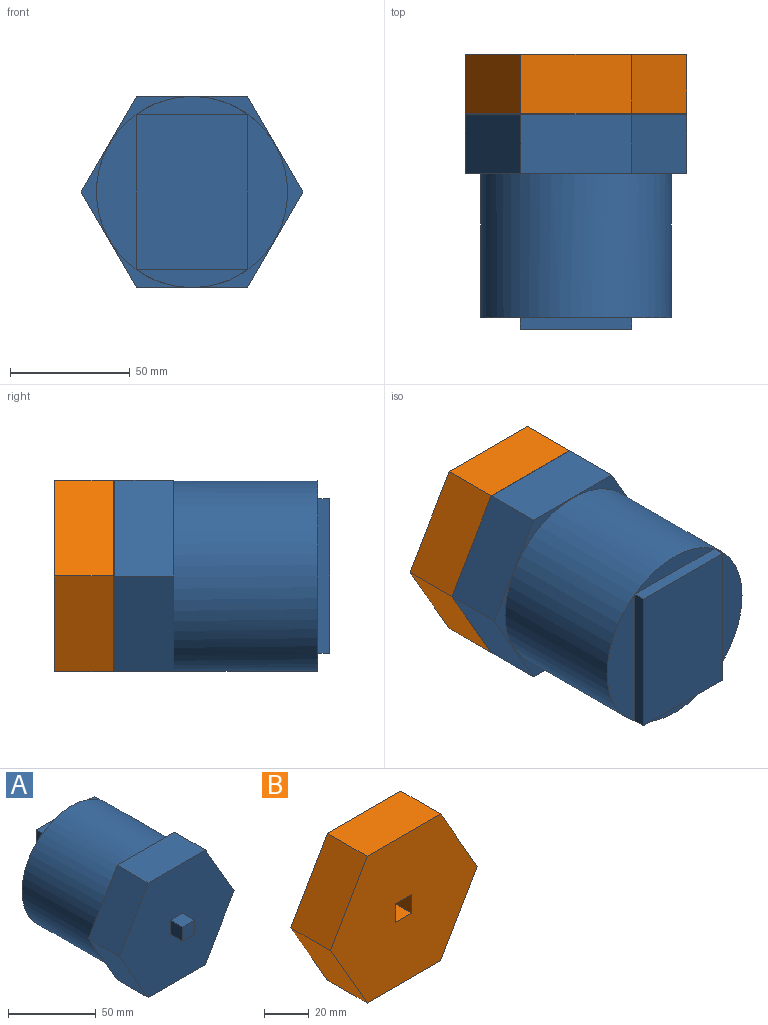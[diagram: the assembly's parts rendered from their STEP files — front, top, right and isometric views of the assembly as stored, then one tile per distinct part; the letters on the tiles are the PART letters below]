
ASSEMBLY  parts=2 mates=1
PART A: 23 faces, bbox 92.4x99.8x80 mm
  f0: plane 64.52x16.49mm, normal (0,1,0), area 745.1mm2, adj f16,f18
  f1: plane 46.61x7.54mm, normal (0,1,0), area 239.1mm2, adj f16,f21
  f2: plane 64.52x16.49mm, normal (0,1,0), area 745.1mm2, adj f16,f20
  f3: plane 92.38x80mm, normal (0,-1,0), area 5446.5mm2, adj f4,f5,f6,f7,f8,f9,f11,f12
  f4: plane 40x25mm, normal (0.87,0,-0.5), area 1154.7mm2, adj f3,f5,f9,f10
  f5: plane 40x25mm, normal (0.87,0,0.5), area 1154.7mm2, adj f3,f4,f6,f10
  f6: plane 46.19x25mm, normal (0,0,1), area 1154.7mm2, adj f3,f5,f7,f10
  f7: plane 40x25mm, normal (-0.87,0,0.5), area 1154.7mm2, adj f3,f6,f8,f10
  f8: plane 40x25mm, normal (-0.87,0,-0.5), area 1154.7mm2, adj f3,f7,f9,f10
  f9: plane 46.19x25mm, normal (0,0,-1), area 1154.7mm2, adj f3,f4,f8,f10
  f10: plane 92.38x80mm, normal (0,1,0), area 566.8mm2, adj f4,f5,f6,f7,f8,f9,f16
  f11: plane 9.8x9.8mm, normal (0,0,-1), area 96mm2, adj f3,f12,f14,f15
  f12: plane 9.8x9.8mm, normal (1,0,0), area 96mm2, adj f3,f11,f13,f15
  f13: plane 9.8x9.8mm, normal (0,0,1), area 96mm2, adj f3,f12,f14,f15
  f14: plane 9.8x9.8mm, normal (-1,0,0), area 96mm2, adj f3,f11,f13,f15
  f15: plane 9.8x9.8mm, normal (0,-1,0), area 96mm2, adj f11,f12,f13,f14
  f16: cylinder r=39.8mm len=79.59mm, axis (0,-1,0), area 15003.2mm2, adj f0,f1,f2,f10,f17
  f17: plane 46.61x7.54mm, normal (0,1,0), area 239.1mm2, adj f16,f19
  f18: plane 64.52x5mm, normal (-1,0,0), area 322.6mm2, adj f0,f19,f21,f22
  f19: plane 46.61x5mm, normal (0,0,1), area 233.1mm2, adj f17,f18,f20,f22
  f20: plane 64.52x5mm, normal (1,0,0), area 322.6mm2, adj f2,f19,f21,f22
  f21: plane 46.61x5mm, normal (0,0,-1), area 233.1mm2, adj f1,f18,f20,f22
  f22: plane 64.52x46.61mm, normal (0,1,0), area 3007.3mm2, adj f18,f19,f20,f21
PART B: 15 faces, bbox 92.4x25x80 mm
  f0: plane 92.38x80mm, normal (0,-1,0), area 5440.6mm2, adj f1,f2,f3,f4,f5,f6,f10,f11
  f1: plane 40x25mm, normal (0.87,0,-0.5), area 1154.7mm2, adj f0,f2,f6,f7
  f2: plane 40x25mm, normal (0.87,0,0.5), area 1154.7mm2, adj f0,f1,f3,f7
  f3: plane 46.19x25mm, normal (0,0,1), area 1154.7mm2, adj f0,f2,f4,f7
  f4: plane 40x25mm, normal (-0.87,0,0.5), area 1154.7mm2, adj f0,f3,f5,f7
  f5: plane 40x25mm, normal (-0.87,0,-0.5), area 1154.7mm2, adj f0,f4,f6,f7
  f6: plane 46.19x25mm, normal (0,0,-1), area 1154.7mm2, adj f0,f1,f5,f7
  f7: plane 92.38x80mm, normal (0,1,0), area 5228.4mm2, adj f1,f2,f3,f4,f5,f6,f8
  f8: cylinder r=10mm len=20mm, axis (0,1,0), area 377mm2, adj f7,f9
  f9: plane 20x20mm, normal (0,1,0), area 314.2mm2, adj f8
  f10: plane 10.1x10.1mm, normal (0,0,1), area 102mm2, adj f0,f11,f13,f14
  f11: plane 10.1x10.1mm, normal (-1,0,0), area 102mm2, adj f0,f10,f12,f14
  f12: plane 10.1x10.1mm, normal (0,0,-1), area 102mm2, adj f0,f11,f13,f14
  f13: plane 10.1x10.1mm, normal (1,0,0), area 102mm2, adj f0,f10,f12,f14
  f14: plane 10.1x10.1mm, normal (0,-1,0), area 102mm2, adj f10,f11,f12,f13
PLACE A rot(axis=(1,0,0),180deg) t=(114.96,-79.9,24.04)mm
PLACE B t=(114.96,-30.2,24.04)mm
MATE planar A.f16 <-> B.f8  axis (0,1,0) through (114.96,-45.1,24.04)mm
